# Revit family: НЕВАТОМ_Нaгреватель NEK-E, Версия 2
name_source: partatom
category: Оборудование
revit_build: Autodesk Revit 2017 (Build: 20170118_1100(x64)
units: mm (PartAtom-declared; Revit-internal decimal feet)

## family parameters
Всегда вертикально = Да
На основе рабочей плоскости = Нет
Общий = Нет
При загрузке вырезать с полостями = Нет
Размер круглого соединителя = Использовать диаметр
Тип детали = Нормальный
Точка расчета площади = Нет

## types (1)
- Нагреватель электрический NEK-E
    A = 315 мм
    ADSK_URL страницы изделия = https://www.nevatom.ru
    ADSK_Единица измерения = шт.
    ADSK_Завод-изготовитель = НЕВАТОМ
    ADSK_Количество = 1
    ADSK_Количество фаз числовое = 3
    ADSK_Коэффициент мощности = 0.548246
    ADSK_Марка = NEK-E 315/18
    ADSK_Масса = 10.7
    ADSK_Наименование = Нагреватель электрический круглый с комплектом автоматики
    ADSK_Напряжение = 380 В
    ADSK_Номинальная мощность = 18 кВт
    ADSK_Полная мощность = 32832 В·А
    ADSK_Примечание = Подбор через ADSK_Номинальная мощность и НЕВАТОМ_Минимальный расход воздуха
    ADSK_Температура воздуха на входе в нагреватель = -37 °C
    ADSK_Температура воздуха на выходе из нагревателя = -10 °C
    ADSK_Ток = 29 А
    B = 660 мм
    B1 = 505 мм
    C = 490 мм
    D = 320 мм
    Dy = 315 мм
    Материал = Сталь оцинкованная
    НЕВАТОМ_NEIVA = NEIVA FPV 2000
    НЕВАТОМ_URL = https://t.me
    НЕВАТОМ_Минимальный расход воздуха = 420.6 м³/ч
    С/3 = 294 мм
    Установка(Predict_1) Преднагрев = см. информацию в каталоге 'Приточно-вытяжные установки', стр. 72
    Установка(Predict_2) Преднагрев = см. информацию в каталоге 'Приточно-вытяжные установки', стр. 72
    Установка(Predict_3) Преднагрев = см. информацию в каталоге 'Приточно-вытяжные установки', стр. 72
